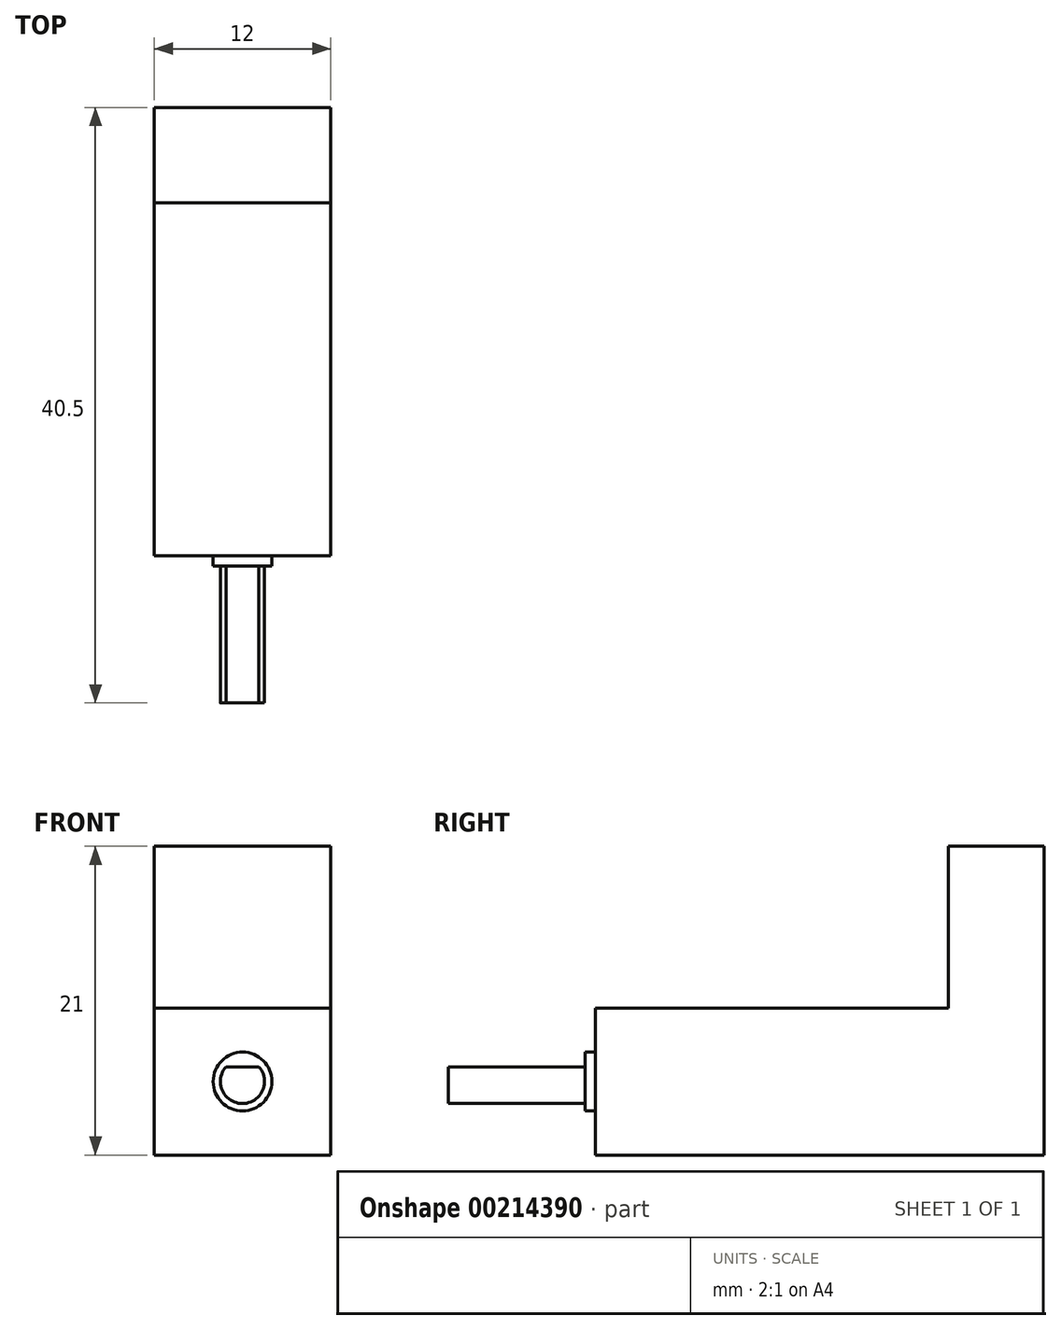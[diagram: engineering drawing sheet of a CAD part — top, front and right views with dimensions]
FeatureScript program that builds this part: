
annotation { "Feature Type Name" : "Feature", "Feature Type Description" : "" }
export const myFeature = defineFeature(function(context is Context, id is Id, definition is map)
    precondition{}
    {
        {
            var Q0;
            Q0=qCreatedBy(makeId("Front.planeOp"),FACE);
            var sketch = newSketch(context, id + "F0", { "sketchPlane" : qUnion([Q0])});
            skLineSegment(sketch, "E0.bottom", {"start": v(-6, 5) * mm, "end": v(6, 5) * mm});
            skLineSegment(sketch, "E0.top", {"start": v(-6, -5) * mm, "end": v(6, -5) * mm});
            skLineSegment(sketch, "E0.left", {"start": v(-6, 5) * mm, "end": v(-6, -5) * mm});
            skLineSegment(sketch, "E0.right", {"start": v(6, 5) * mm, "end": v(6, -5) * mm});
            skSolve(sketch);
        }
        {
            var Q0;
            Q0 = qSketchRegion(id + "F0", true);
            extrude(context, id + "F1", {"entities" : qUnion([Q0]), "depth" : 30.5 * mm});
        }
        {
            var Q0;
            Q0=makeQuery(id+"F1.opExtrude","CAP_FACE",FACE,{"disambiguationData":[OSD([sQuery(id+"F0.wireOp",EDGE,"E0.bottom"),sQuery(id+"F0.wireOp",EDGE,"E0.top"),sQuery(id+"F0.wireOp",EDGE,"E0.left"),sQuery(id+"F0.wireOp",EDGE,"E0.right")])],"isStart":false});
            var sketch = newSketch(context, id + "F2", { "sketchPlane" : qUnion([Q0])});
            skCircle(sketch, "E1", {"center": v(0, 0) * mm, "radius": 2 * mm});
            skSolve(sketch);
        }
        {
            var Q0;
            Q0 = qSketchRegion(id + "F2", true);
            extrude(context, id + "F3", {"entities" : qUnion([Q0]), "operationType" : NewBodyOperationType.ADD, "depth" : .7 * mm});
        }
        {
            var Q0;
            Q0=makeQuery(id+"F3.opExtrude","CAP_FACE",FACE,{"disambiguationData":[OSD([sQuery(id+"F2.wireOp",EDGE,"E1")])],"isStart":false});
            var sketch = newSketch(context, id + "F4", { "sketchPlane" : qUnion([Q0])});
            skCircle(sketch, "E2", {"center": v(0, 0) * mm, "radius": 1.5 * mm});
            skSolve(sketch);
        }
        {
            var Q0;
            Q0 = qSketchRegion(id + "F4", true);
            extrude(context, id + "F5", {"entities" : qUnion([Q0]), "operationType" : NewBodyOperationType.ADD, "depth" : 9.3 * mm});
        }
        {
            var Q0;
            Q0=makeQuery(id+"F5.opExtrude","CAP_FACE",FACE,{"disambiguationData":[OSD([sQuery(id+"F4.wireOp",EDGE,"E2")])],"isStart":false});
            var sketch = newSketch(context, id + "F6", { "sketchPlane" : qUnion([Q0])});
            skLineSegment(sketch, "E3.bottom", {"start": v(-3.12, 1) * mm, "end": v(3.57, 1) * mm});
            skLineSegment(sketch, "E3.top", {"start": v(-3.12, 2.68) * mm, "end": v(3.57, 2.68) * mm});
            skLineSegment(sketch, "E3.left", {"start": v(-3.12, 1) * mm, "end": v(-3.12, 2.68) * mm});
            skLineSegment(sketch, "E3.right", {"start": v(3.57, 1) * mm, "end": v(3.57, 2.68) * mm});
            skSolve(sketch);
        }
        {
            var Q0;
            Q0 = qSketchRegion(id + "F6", true);
            extrude(context, id + "F7", {"entities" : qUnion([Q0]), "operationType" : NewBodyOperationType.REMOVE, "oppositeDirection" : true, "depth" : 9.3 * mm});
        }
        {
            var Q0;
            Q0=makeQuery(id+"F1.opExtrude","SWEPT_FACE",FACE,{"disambiguationData":[OSD([sQuery(id+"F0.wireOp",EDGE,"E0.bottom")])]});
            var sketch = newSketch(context, id + "F8", { "sketchPlane" : qUnion([Q0])});
            skLineSegment(sketch, "E4.bottom", {"start": v(6, 0) * mm, "end": v(-6, 0) * mm});
            skLineSegment(sketch, "E4.top", {"start": v(6, -6.5) * mm, "end": v(-6, -6.5) * mm});
            skLineSegment(sketch, "E4.left", {"start": v(6, 0) * mm, "end": v(6, -6.5) * mm});
            skLineSegment(sketch, "E4.right", {"start": v(-6, 0) * mm, "end": v(-6, -6.5) * mm});
            skSolve(sketch);
        }
        {
            var Q0;
            Q0 = qSketchRegion(id + "F8", true);
            extrude(context, id + "F9", {"entities" : qUnion([Q0]), "operationType" : NewBodyOperationType.ADD, "depth" : 11 * mm});
        }
    });
